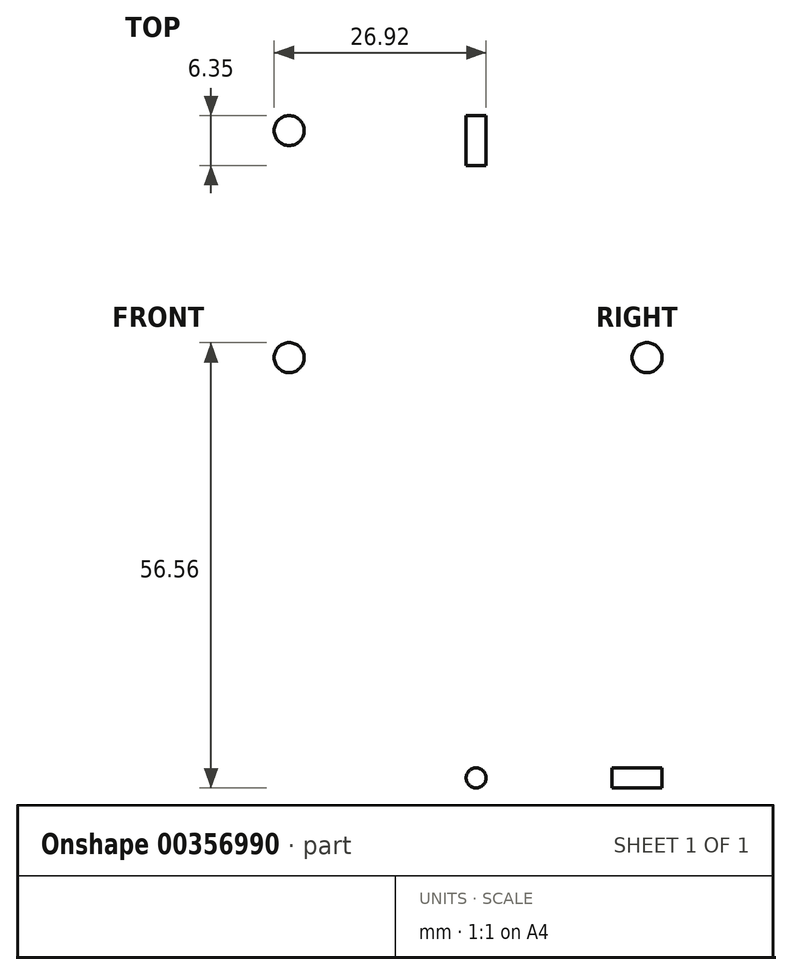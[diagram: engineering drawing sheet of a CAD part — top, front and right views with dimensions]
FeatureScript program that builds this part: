
annotation { "Feature Type Name" : "Feature", "Feature Type Description" : "" }
export const myFeature = defineFeature(function(context is Context, id is Id, definition is map)
    precondition{}
    {
        {
            var Q0;
            Q0=qCreatedBy(makeId("Front.planeOp"),FACE);
            var sketch = newSketch(context, id + "F0", { "sketchPlane" : qUnion([Q0])});
            skCircle(sketch, "E0", {"center": v(-37.37, -26.23) * mm, "radius": 1.27 * mm});
            skCircle(sketch, "E1", {"center": v(-61.11, 27.16) * mm, "radius": 1.9 * mm});
            skSolve(sketch);
        }
        {
            var Q0;
            Q0=makeQuery(id+"F0.imprint","IMPRINT",FACE,{"disambiguationData":[TD([[makeQuery(id+"F0.imprint","IMPRINT",EDGE,{"derivedFrom":sQuery(id+"F0.wireOp",EDGE,"E0")}),1.0]])]});
            extrude(context, id + "F1", {"entities" : qUnion([Q0]), "depth" : 6.35 * mm});
        }
        {
            var Q0;
            Q0 = qSketchRegion(id + "F0", true);
            extrude(context, id + "F2", {"entities" : qUnion([Q0]), "operationType" : NewBodyOperationType.ADD, "depth" : 3.8 * mm});
        }
        {
            var Q0;
            Q0=makeQuery(id+"F2.opExtrude","CAP_FACE",FACE,{"disambiguationData":[OSD([sQuery(id+"F0.wireOp",EDGE,"E1")])],"isStart":true});
            var Q1;
            Q1=makeQuery(id+"F2.opExtrude","CAP_EDGE",EDGE,{"disambiguationData":[OSD([sQuery(id+"F0.wireOp",EDGE,"E1")])],"isStart":false});
            fillet(context, id + "F3", {"entities" : qUnion([Q0, Q1]), "radius" : 1.9 * mm, "tangentPropagation" : true, "allowEdgeOverflow" : false});
        }
    });
